# Revit family: Domotics-DomesticRanges-GEWISS-SYSTEM_COMMAND-PUSH-BUTTON_2M
name_source: partatom
category: Apparecchi elettrici
revit_build: Autodesk Revit 2016 (Build: 20161004_0715(x64)
units: mm (PartAtom-declared; Revit-internal decimal feet)

## family parameters
Condiviso = Sì
Host = Superficie
Mantenere orientamento annotazione = Sì
Numero OmniClass = 23.80.50.11.14
Punto di calcolo locali = Sì
Quota connettore circolare = Usa diametro
Taglio con vuoti quando caricato = Sì
Tipo di parte = Normale
Titolo OmniClass = Switches

## types (2) — shared parameters
Button key = With diffuser
Carico apparente = 0 VA
Catalogue = DOMOTICS
Catalogue Range = SYSTEM - DOMESTIC RANGE
Description. = Push-button
Description: = 1P NO - 10 A - illuminable
Electrocod = 0130
IDF = e4d342d5-c706-4085-a83c-f71295e5c4cb
IDT = dfebf16c-f340-4440-887a-18929c4062cc
Immagine tipo = GW21527.jpg
Larghezza pulsante = 46 mm  [stored 0.150919 ft]
N. poli = 1
No. SYSTEM modules = 2
Produttore = GEWISS S.p.A.
Prospetto di default = 1219 mm
SEO = Push button
Simbolo = SIMBOLO PULSANTI : PULSANTE
Technical sheet = https://www.gewiss.com
Tipo_ = SYSTEM PULSANTI 2M_BASE : GW21527 - Nero
Type = Push-button
URL = https://www.gewiss.com
Version file RFA = 19.4
Volt = 230 V
Voltage = 250 V ac
Voltage: = 250 V ac

## per-type parameters (varying)
| type | Colour | Descrizione | EAN code | Modello |
| GW20527 - Push-button-1P NO 10A 2M illum.white | White | PUSH-BUTTON-1P NO 10A 2M ILLUM.SY/WT | 8011564184626 | GW20527 |
| GW21527 - Push-button-1P NO 10A 2M illum.black | Black | PUSH-BUTTON-1P NA 10A 2M ILLUM.SY/BK | 8011564184633 | GW21527 |

note: [stored X ft] marks values corroborated as IEEE doubles in the binary element streams (Revit-internal decimal feet)

## geometry (parser evidence)
native form markers: Sweep x2
no freeform markers — native parametric forms only
